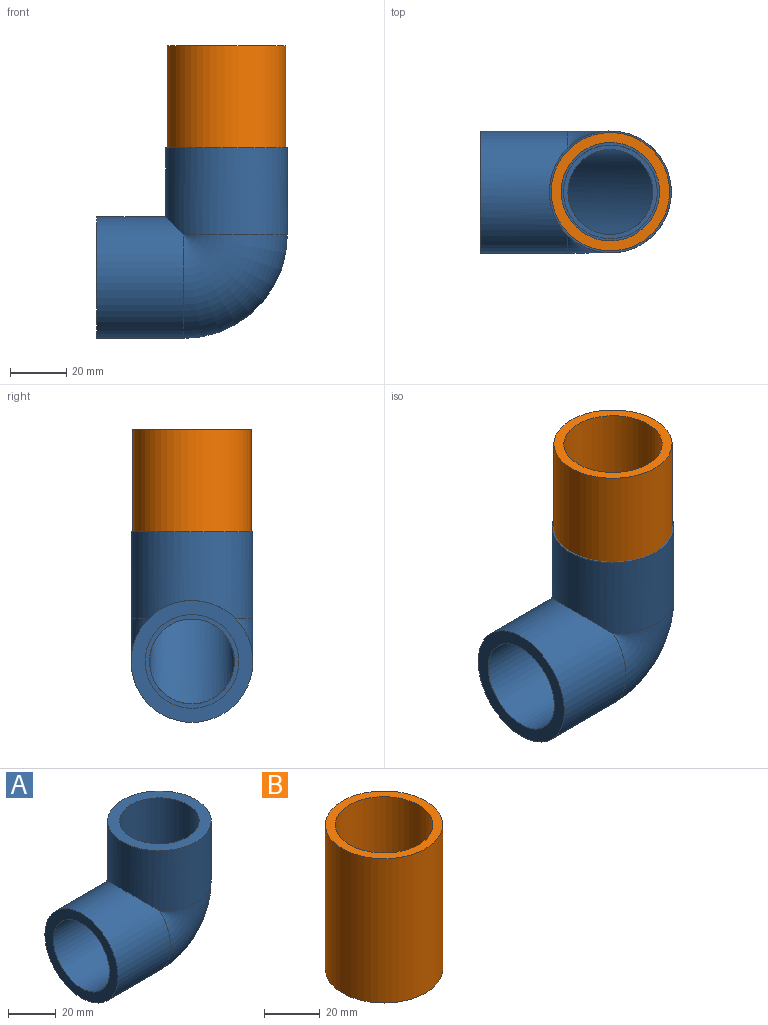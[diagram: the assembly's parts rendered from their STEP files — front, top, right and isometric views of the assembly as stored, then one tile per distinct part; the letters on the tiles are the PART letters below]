
ASSEMBLY  parts=2 mates=1
PART A: 12 faces, bbox 67.9x43.4x67.9 mm
  f0: cylinder r=15.14mm len=30.28mm, axis (-1,0,0), area 219.9mm2, adj f7,f11
  f1: cylinder r=15.14mm len=30.28mm, axis (0,0,1), area 219.9mm2, adj f7,f8
  f2: plane 43.43x43.43mm, normal (-1,0,0), area 605.5mm2, adj f5,f10
  f3: cylinder r=21.72mm len=43.43mm, axis (0,0,-1), area 4091.6mm2, adj f4,f5,f6
  f4: plane 43.43x43.43mm, normal (0,0,1), area 605.5mm2, adj f3,f9
  f5: cylinder r=21.72mm len=43.43mm, axis (1,0,0), area 4091.6mm2, adj f2,f3,f6
  f6: torus R=15.14mm, axis (0,1,0), area 3481.4mm2, adj f3,f5
  f7: torus R=15.14mm, axis (0,1,0), area 2261.8mm2, adj f0,f1
  f8: plane 33.4x33.4mm, normal (0,0,1), area 156.2mm2, adj f1,f9
  f9: cylinder r=16.7mm len=33.4mm, axis (0,0,1), area 3019.8mm2, adj f4,f8
  f10: cylinder r=16.7mm len=33.4mm, axis (-1,0,0), area 3019.8mm2, adj f2,f11
  f11: plane 33.4x33.4mm, normal (-1,0,0), area 156.2mm2, adj f0,f10
PART B: 4 faces, bbox 42.2x42.2x63.5 mm
  f0: cylinder r=17.53mm len=63.5mm, axis (0,0,-1), area 6992.6mm2, adj f2,f3
  f1: cylinder r=21.08mm len=63.5mm, axis (0,0,-1), area 8411.3mm2, adj f2,f3
  f2: plane 42.16x42.16mm, normal (0,0,1), area 431.3mm2, adj f0,f1
  f3: plane 42.16x42.16mm, normal (0,0,-1), area 431.3mm2, adj f0,f1
PLACE A t=(-49.38,-3.51,-23.11)mm
PLACE B t=(-49.38,-3.51,-3.97)mm
MATE fastened A.f3 <-> B.f1  axis (0,0,1) through (-49.38,-3.51,8.73)mm
